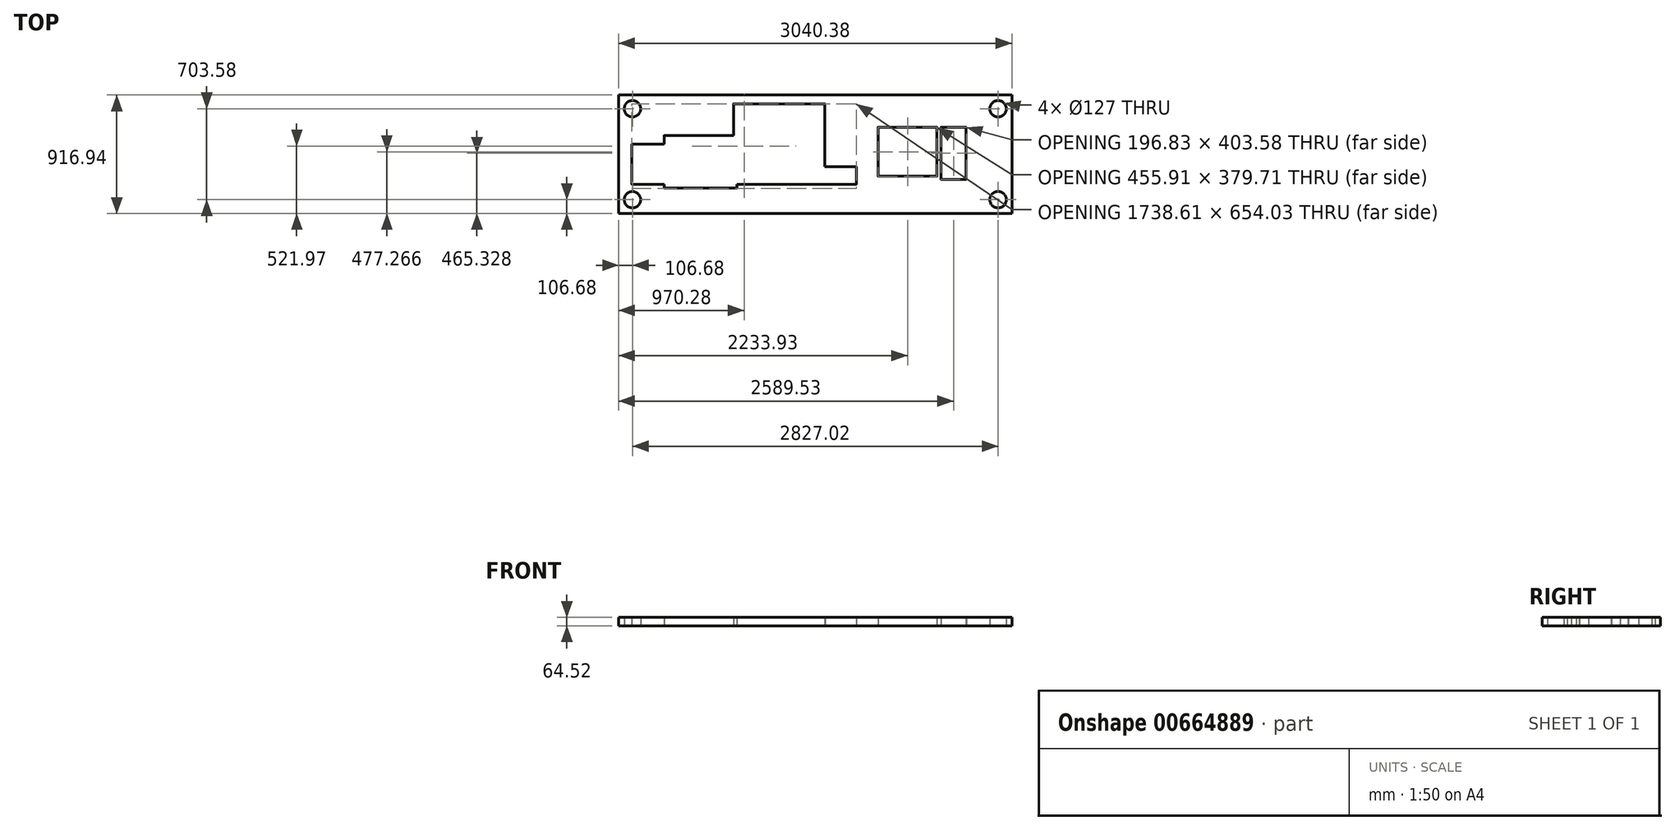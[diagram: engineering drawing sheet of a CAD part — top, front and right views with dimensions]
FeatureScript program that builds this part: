
annotation { "Feature Type Name" : "Feature", "Feature Type Description" : "" }
export const myFeature = defineFeature(function(context is Context, id is Id, definition is map)
    precondition{}
    {
        {
            var Q0;
            Q0=qCreatedBy(makeId("Top.planeOp"),FACE);
            var sketch = newSketch(context, id + "F0", { "sketchPlane" : qUnion([Q0])});
            skLineSegment(sketch, "E0", {"start": v(-1520.2, -458.47) * mm, "end": v(1520.19, -458.47) * mm});
            skLineSegment(sketch, "E1", {"start": v(1520.19, -458.47) * mm, "end": v(1520.19, 458.47) * mm});
            skLineSegment(sketch, "E2", {"start": v(1520.19, 458.47) * mm, "end": v(-1520.19, 458.47) * mm});
            skLineSegment(sketch, "E3", {"start": v(-1520.2, 458.47) * mm, "end": v(-1520.2, -458.47) * mm});
            skLineSegment(sketch, "E4", {"start": v(-1418.6, -232.41) * mm, "end": v(-1167.13, -232.41) * mm});
            skArc(sketch, "E5", {"start": v(-1167.13, -233.05) * mm, "mid": v(-1166.5, -232.41) * mm, "end": v(-1167.13, -231.78) * mm});
            skArc(sketch, "E6", {"start": v(-1418.6, -231.78) * mm, "mid": v(-1419.23, -232.41) * mm, "end": v(-1418.6, -233.05) * mm});
            skLineSegment(sketch, "E7", {"start": v(-1418.6, -232.41) * mm, "end": v(-1418.6, 77.47) * mm});
            skArc(sketch, "E8", {"start": v(-1417.96, 77.47) * mm, "mid": v(-1418.6, 78.1) * mm, "end": v(-1419.23, 77.47) * mm});
            skArc(sketch, "E9", {"start": v(-1419.23, -232.41) * mm, "mid": v(-1418.6, -233.05) * mm, "end": v(-1417.96, -232.41) * mm});
            skLineSegment(sketch, "E10", {"start": v(-1418.6, 77.47) * mm, "end": v(-1167.13, 77.47) * mm});
            skArc(sketch, "E11", {"start": v(-1167.13, 76.83) * mm, "mid": v(-1166.5, 77.47) * mm, "end": v(-1167.13, 78.1) * mm});
            skArc(sketch, "E12", {"start": v(-1418.6, 78.1) * mm, "mid": v(-1419.23, 77.47) * mm, "end": v(-1418.6, 76.83) * mm});
            skLineSegment(sketch, "E13", {"start": v(-1167.13, -262.9) * mm, "end": v(-605.8, -262.9) * mm});
            skArc(sketch, "E14", {"start": v(-605.8, -263.53) * mm, "mid": v(-605.15, -262.9) * mm, "end": v(-605.8, -262.26) * mm});
            skArc(sketch, "E15", {"start": v(-1167.13, -262.26) * mm, "mid": v(-1167.77, -262.9) * mm, "end": v(-1167.13, -263.53) * mm});
            skLineSegment(sketch, "E16", {"start": v(-1167.13, -232.41) * mm, "end": v(-1167.13, -262.9) * mm});
            skArc(sketch, "E17", {"start": v(-1167.77, -262.9) * mm, "mid": v(-1167.13, -263.53) * mm, "end": v(-1166.5, -262.9) * mm});
            skArc(sketch, "E18", {"start": v(-1166.5, -232.41) * mm, "mid": v(-1167.13, -231.78) * mm, "end": v(-1167.77, -232.41) * mm});
            skLineSegment(sketch, "E19", {"start": v(-1167.13, 146.05) * mm, "end": v(-1167.13, 77.47) * mm});
            skArc(sketch, "E20", {"start": v(-1167.77, 77.47) * mm, "mid": v(-1167.13, 76.83) * mm, "end": v(-1166.5, 77.47) * mm});
            skArc(sketch, "E21", {"start": v(-1166.5, 146.05) * mm, "mid": v(-1167.13, 146.68) * mm, "end": v(-1167.77, 146.05) * mm});
            skLineSegment(sketch, "E22", {"start": v(-1167.13, 146.05) * mm, "end": v(-631.2, 146.05) * mm});
            skArc(sketch, "E23", {"start": v(-631.2, 145.41) * mm, "mid": v(-630.56, 146.05) * mm, "end": v(-631.2, 146.68) * mm});
            skArc(sketch, "E24", {"start": v(-1167.13, 146.68) * mm, "mid": v(-1167.77, 146.05) * mm, "end": v(-1167.13, 145.41) * mm});
            skLineSegment(sketch, "E25", {"start": v(-631.2, 389.9) * mm, "end": v(74.93, 389.9) * mm});
            skArc(sketch, "E26", {"start": v(74.93, 389.25) * mm, "mid": v(75.56, 389.9) * mm, "end": v(74.93, 390.53) * mm});
            skArc(sketch, "E27", {"start": v(-631.2, 390.53) * mm, "mid": v(-631.83, 389.9) * mm, "end": v(-631.2, 389.25) * mm});
            skLineSegment(sketch, "E28", {"start": v(-631.2, 389.9) * mm, "end": v(-631.2, 146.05) * mm});
            skArc(sketch, "E29", {"start": v(-631.83, 146.05) * mm, "mid": v(-631.2, 145.41) * mm, "end": v(-630.56, 146.05) * mm});
            skArc(sketch, "E30", {"start": v(-630.56, 389.9) * mm, "mid": v(-631.2, 390.53) * mm, "end": v(-631.83, 389.9) * mm});
            skLineSegment(sketch, "E31", {"start": v(-605.8, -232.41) * mm, "end": v(-605.8, -262.9) * mm});
            skArc(sketch, "E32", {"start": v(-606.43, -262.9) * mm, "mid": v(-605.8, -263.53) * mm, "end": v(-605.15, -262.9) * mm});
            skArc(sketch, "E33", {"start": v(-605.15, -232.41) * mm, "mid": v(-605.8, -231.78) * mm, "end": v(-606.43, -232.41) * mm});
            skLineSegment(sketch, "E34", {"start": v(-605.8, -232.41) * mm, "end": v(318.77, -232.41) * mm});
            skArc(sketch, "E35", {"start": v(318.77, -233.05) * mm, "mid": v(319.4, -232.41) * mm, "end": v(318.77, -231.78) * mm});
            skArc(sketch, "E36", {"start": v(-605.8, -231.78) * mm, "mid": v(-606.43, -232.41) * mm, "end": v(-605.8, -233.05) * mm});
            skLineSegment(sketch, "E37", {"start": v(74.93, 389.9) * mm, "end": v(74.93, -97.79) * mm});
            skArc(sketch, "E38", {"start": v(74.3, -97.8) * mm, "mid": v(74.93, -98.42) * mm, "end": v(75.56, -97.8) * mm});
            skArc(sketch, "E39", {"start": v(75.56, 389.9) * mm, "mid": v(74.93, 390.53) * mm, "end": v(74.3, 389.9) * mm});
            skLineSegment(sketch, "E40", {"start": v(74.93, -97.8) * mm, "end": v(318.77, -97.8) * mm});
            skArc(sketch, "E41", {"start": v(318.77, -98.42) * mm, "mid": v(319.4, -97.8) * mm, "end": v(318.77, -97.16) * mm});
            skArc(sketch, "E42", {"start": v(74.93, -97.16) * mm, "mid": v(74.3, -97.8) * mm, "end": v(74.93, -98.42) * mm});
            skLineSegment(sketch, "E43", {"start": v(318.77, -232.41) * mm, "end": v(318.77, -97.8) * mm});
            skArc(sketch, "E44", {"start": v(319.4, -97.8) * mm, "mid": v(318.77, -97.16) * mm, "end": v(318.13, -97.8) * mm});
            skArc(sketch, "E45", {"start": v(318.13, -232.41) * mm, "mid": v(318.77, -233.05) * mm, "end": v(319.4, -232.41) * mm});
            skLineSegment(sketch, "E46", {"start": v(486.4, -170.43) * mm, "end": v(941.07, -170.43) * mm});
            skArc(sketch, "E47", {"start": v(941.07, -171.07) * mm, "mid": v(941.7, -170.43) * mm, "end": v(941.07, -169.8) * mm});
            skArc(sketch, "E48", {"start": v(486.4, -169.8) * mm, "mid": v(485.77, -170.43) * mm, "end": v(486.4, -171.07) * mm});
            skLineSegment(sketch, "E49", {"start": v(486.4, -170.43) * mm, "end": v(486.4, 208.03) * mm});
            skArc(sketch, "E50", {"start": v(487.04, 208.03) * mm, "mid": v(486.4, 208.66) * mm, "end": v(485.77, 208.03) * mm});
            skArc(sketch, "E51", {"start": v(485.77, -170.43) * mm, "mid": v(486.4, -171.07) * mm, "end": v(487.04, -170.43) * mm});
            skLineSegment(sketch, "E52", {"start": v(486.4, 208.03) * mm, "end": v(941.07, 208.03) * mm});
            skArc(sketch, "E53", {"start": v(941.07, 207.4) * mm, "mid": v(941.7, 208.03) * mm, "end": v(941.07, 208.66) * mm});
            skArc(sketch, "E54", {"start": v(486.4, 208.66) * mm, "mid": v(485.77, 208.03) * mm, "end": v(486.4, 207.4) * mm});
            skLineSegment(sketch, "E55", {"start": v(941.07, -170.43) * mm, "end": v(941.07, 208.03) * mm});
            skArc(sketch, "E56", {"start": v(941.7, 208.03) * mm, "mid": v(941.07, 208.66) * mm, "end": v(940.44, 208.03) * mm});
            skArc(sketch, "E57", {"start": v(940.44, -170.43) * mm, "mid": v(941.07, -171.07) * mm, "end": v(941.7, -170.43) * mm});
            skLineSegment(sketch, "E58", {"start": v(971.55, -194.31) * mm, "end": v(1167.13, -194.31) * mm});
            skArc(sketch, "E59", {"start": v(1167.13, -194.95) * mm, "mid": v(1167.77, -194.31) * mm, "end": v(1167.13, -193.68) * mm});
            skArc(sketch, "E60", {"start": v(971.55, -193.68) * mm, "mid": v(970.92, -194.31) * mm, "end": v(971.55, -194.95) * mm});
            skLineSegment(sketch, "E61", {"start": v(971.55, -194.31) * mm, "end": v(971.55, 208.03) * mm});
            skArc(sketch, "E62", {"start": v(972.19, 208.03) * mm, "mid": v(971.55, 208.66) * mm, "end": v(970.92, 208.03) * mm});
            skArc(sketch, "E63", {"start": v(970.92, -194.31) * mm, "mid": v(971.55, -194.95) * mm, "end": v(972.19, -194.31) * mm});
            skLineSegment(sketch, "E64", {"start": v(1167.13, -194.31) * mm, "end": v(1167.13, 208.03) * mm});
            skArc(sketch, "E65", {"start": v(1167.77, 208.03) * mm, "mid": v(1167.13, 208.66) * mm, "end": v(1166.5, 208.03) * mm});
            skArc(sketch, "E66", {"start": v(1166.5, -194.31) * mm, "mid": v(1167.13, -194.95) * mm, "end": v(1167.77, -194.31) * mm});
            skLineSegment(sketch, "E67", {"start": v(971.55, 208.03) * mm, "end": v(1167.13, 208.03) * mm});
            skArc(sketch, "E68", {"start": v(1167.13, 207.4) * mm, "mid": v(1167.77, 208.03) * mm, "end": v(1167.13, 208.66) * mm});
            skArc(sketch, "E69", {"start": v(971.55, 208.66) * mm, "mid": v(970.92, 208.03) * mm, "end": v(971.55, 207.4) * mm});
            skArc(sketch, "E70", {"start": v(-1413.51, -415.3) * mm, "mid": v(-1350.01, -351.8) * mm, "end": v(-1413.51, -288.3) * mm});
            skArc(sketch, "E71", {"start": v(-1413.51, -288.3) * mm, "mid": v(-1477.01, -351.8) * mm, "end": v(-1413.51, -415.3) * mm});
            skArc(sketch, "E72", {"start": v(1413.5, -415.3) * mm, "mid": v(1477, -351.8) * mm, "end": v(1413.5, -288.3) * mm});
            skArc(sketch, "E73", {"start": v(1413.5, -288.3) * mm, "mid": v(1350, -351.8) * mm, "end": v(1413.5, -415.3) * mm});
            skArc(sketch, "E74", {"start": v(1413.5, 288.3) * mm, "mid": v(1477, 351.8) * mm, "end": v(1413.5, 415.3) * mm});
            skArc(sketch, "E75", {"start": v(1413.5, 415.3) * mm, "mid": v(1350, 351.8) * mm, "end": v(1413.5, 288.3) * mm});
            skArc(sketch, "E76", {"start": v(-1413.51, 288.3) * mm, "mid": v(-1350.01, 351.8) * mm, "end": v(-1413.51, 415.3) * mm});
            skArc(sketch, "E77", {"start": v(-1413.51, 415.3) * mm, "mid": v(-1477.01, 351.8) * mm, "end": v(-1413.51, 288.3) * mm});
            skSolve(sketch);
        }
        {
            var Q0;
            Q0=makeQuery(id+"F0.imprint","IMPRINT",FACE,{"disambiguationData":[TD([[makeQuery(id+"F0.imprint","IMPRINT",EDGE,{"derivedFrom":sQuery(id+"F0.wireOp",EDGE,"E0")}),1.0]])]});
            extrude(context, id + "F1", {"entities" : qUnion([Q0]), "depth" : 64.52 * mm, "offsetDistance" : 25.4 * mm});
        }
    });
